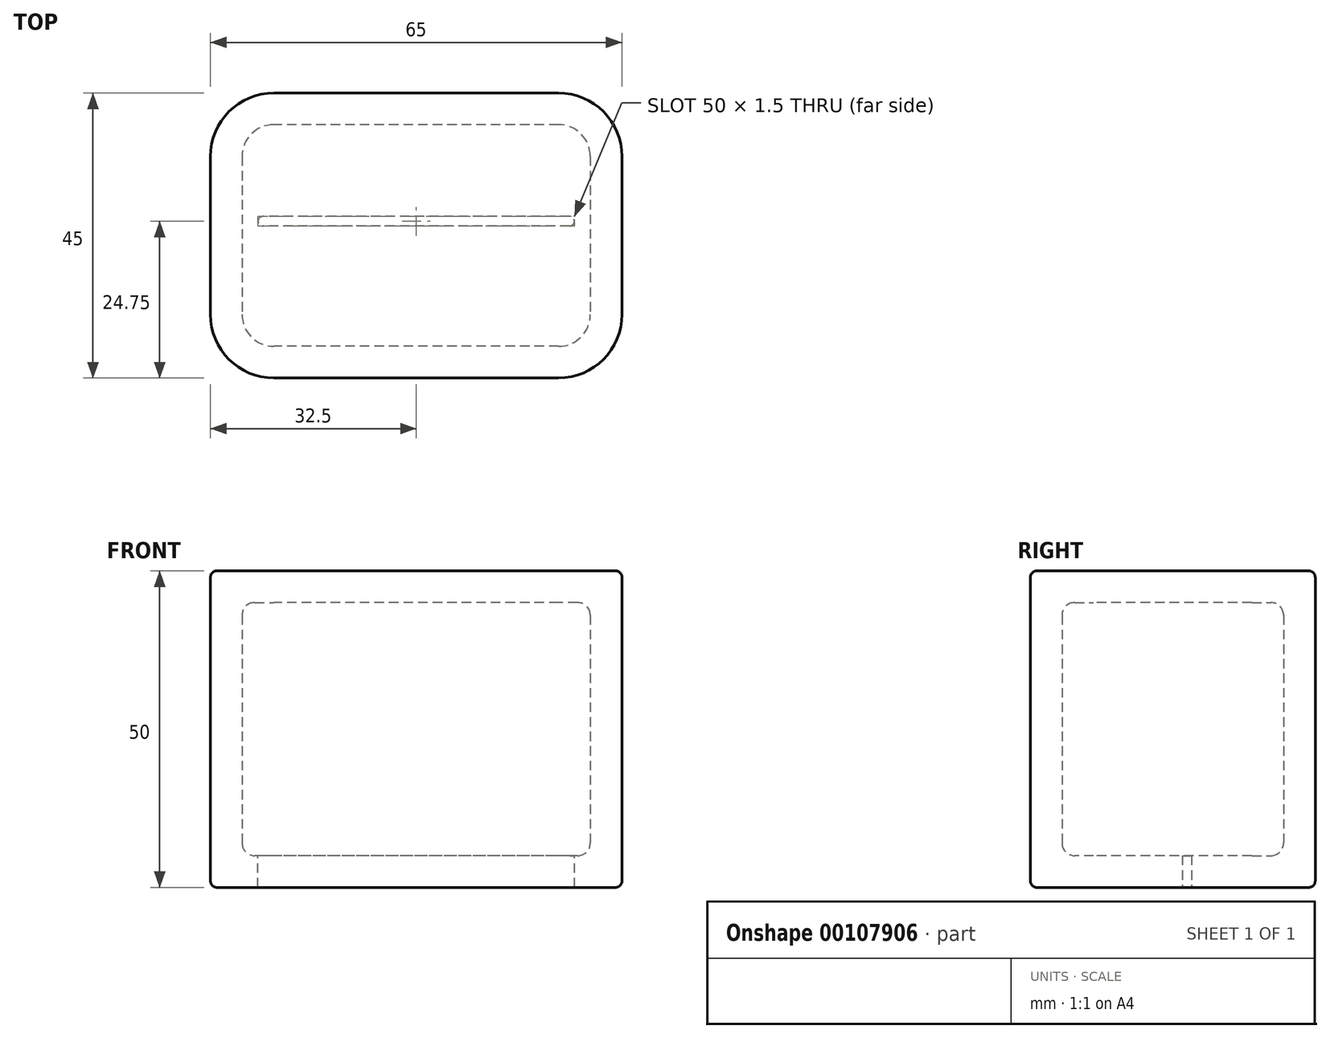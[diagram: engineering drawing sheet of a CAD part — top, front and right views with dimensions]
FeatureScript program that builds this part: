
annotation { "Feature Type Name" : "Feature", "Feature Type Description" : "" }
export const myFeature = defineFeature(function(context is Context, id is Id, definition is map)
    precondition{}
    {
        {
            var Q0;
            Q0=qCreatedBy(makeId("Top.planeOp"),FACE);
            var sketch = newSketch(context, id + "F0", { "sketchPlane" : qUnion([Q0])});
            skPoint(sketch, "E0.middle", {"position": v(0, 0) * mm});
            skLineSegment(sketch, "E1.bottom", {"start": v(32.5, 22.5) * mm, "end": v(-32.5, 22.5) * mm});
            skLineSegment(sketch, "E1.top", {"start": v(32.5, -22.5) * mm, "end": v(-32.5, -22.5) * mm});
            skLineSegment(sketch, "E1.left", {"start": v(32.5, 22.5) * mm, "end": v(32.5, -22.5) * mm});
            skLineSegment(sketch, "E1.right", {"start": v(-32.5, 22.5) * mm, "end": v(-32.5, -22.5) * mm});
            skLineSegment(sketch, "E2.bottom", {"start": v(-27.5, -17.5) * mm, "end": v(27.5, -17.5) * mm, "construction": true});
            skLineSegment(sketch, "E2.top", {"start": v(-27.5, 17.5) * mm, "end": v(27.5, 17.5) * mm, "construction": true});
            skLineSegment(sketch, "E2.left", {"start": v(-27.5, -17.5) * mm, "end": v(-27.5, 17.5) * mm, "construction": true});
            skLineSegment(sketch, "E2.right", {"start": v(27.5, -17.5) * mm, "end": v(27.5, 17.5) * mm, "construction": true});
            skLineSegment(sketch, "E3", {"start": v(-32.5, -17.5) * mm, "end": v(-27.5, -17.5) * mm, "construction": true});
            skLineSegment(sketch, "E4", {"start": v(-27.5, -17.5) * mm, "end": v(-27.5, -22.5) * mm, "construction": true});
            skSolve(sketch);
        }
        {
            var Q0;
            Q0=makeQuery(id+"F0.imprint","IMPRINT",FACE,{"disambiguationData":[TD([[makeQuery(id+"F0.imprint","IMPRINT",EDGE,{"derivedFrom":sQuery(id+"F0.wireOp",EDGE,"E1.bottom")}),1.0]])]});
            extrude(context, id + "F1", {"entities" : qUnion([Q0]), "depth" : 50 * mm});
        }
        {
            var Q0;
            Q0=makeQuery(id+"F1.opExtrude","SWEPT_EDGE",EDGE,{"disambiguationData":[OSD([sQuery(id+"F0.wireOp",EDGE,"E1.top"),sQuery(id+"F0.wireOp",EDGE,"E1.left")])]});
            var Q1;
            Q1=makeQuery(id+"F1.opExtrude","SWEPT_EDGE",EDGE,{"disambiguationData":[OSD([sQuery(id+"F0.wireOp",EDGE,"E1.top"),sQuery(id+"F0.wireOp",EDGE,"E1.right")])]});
            var Q2;
            Q2=makeQuery(id+"F1.opExtrude","SWEPT_EDGE",EDGE,{"disambiguationData":[OSD([sQuery(id+"F0.wireOp",EDGE,"E1.bottom"),sQuery(id+"F0.wireOp",EDGE,"E1.right")])]});
            var Q3;
            Q3=makeQuery(id+"F1.opExtrude","SWEPT_EDGE",EDGE,{"disambiguationData":[OSD([sQuery(id+"F0.wireOp",EDGE,"E1.bottom"),sQuery(id+"F0.wireOp",EDGE,"E1.left")])]});
            fillet(context, id + "F2", {"entities" : qUnion([Q0, Q1, Q2, Q3]), "radius" : 10 * mm, "tangentPropagation" : true, "allowEdgeOverflow" : false});
        }
        {
            var Q0;
            Q0=makeQuery(id+"F1.opExtrude","CAP_FACE",FACE,{"disambiguationData":[OSD([sQuery(id+"F0.wireOp",EDGE,"E1.bottom"),sQuery(id+"F0.wireOp",EDGE,"E1.top"),sQuery(id+"F0.wireOp",EDGE,"E1.left"),sQuery(id+"F0.wireOp",EDGE,"E1.right")])],"isStart":false});
            var Q1;
            Q1=makeQuery(id+"F1.opExtrude","SWEPT_BODY",BODY,{"disambiguationData":[OSD([sQuery(id+"F0.wireOp",EDGE,"E1.bottom"),sQuery(id+"F0.wireOp",EDGE,"E1.top"),sQuery(id+"F0.wireOp",EDGE,"E1.left"),sQuery(id+"F0.wireOp",EDGE,"E1.right")])]});
            shell(context, id + "F3", {"isHollow" : true, "entities" : qUnion([Q0]), "parts" : qUnion([Q1]), "thickness" : 5 * mm});
        }
        {
            var Q0;
            Q0=makeQuery(id+"F1.opExtrude","CAP_FACE",FACE,{"disambiguationData":[OSD([sQuery(id+"F0.wireOp",EDGE,"E1.bottom"),sQuery(id+"F0.wireOp",EDGE,"E1.top"),sQuery(id+"F0.wireOp",EDGE,"E1.left"),sQuery(id+"F0.wireOp",EDGE,"E1.right")])],"isStart":true});
            var sketch = newSketch(context, id + "F4", { "sketchPlane" : qUnion([Q0])});
            skLineSegment(sketch, "E5.bottom", {"start": v(25, -1.5) * mm, "end": v(-25, -1.5) * mm});
            skLineSegment(sketch, "E5.top", {"start": v(25, -3) * mm, "end": v(-25, -3) * mm});
            skLineSegment(sketch, "E5.left", {"start": v(25, -1.5) * mm, "end": v(25, -3) * mm});
            skLineSegment(sketch, "E5.right", {"start": v(-25, -1.5) * mm, "end": v(-25, -3) * mm});
            skSolve(sketch);
        }
        {
            var Q0;
            Q0=makeQuery(id+"F4.imprint","IMPRINT",FACE,{"disambiguationData":[TD([[makeQuery(id+"F4.imprint","IMPRINT",EDGE,{"derivedFrom":sQuery(id+"F4.wireOp",EDGE,"E5.bottom")}),1.0]])]});
            extrude(context, id + "F5", {"entities" : qUnion([Q0]), "operationType" : NewBodyOperationType.REMOVE, "endBound" : BoundingType.UP_TO_NEXT, "oppositeDirection" : true, "depth" : 11.66 * mm});
        }
        {
            var Q0;
            Q0=makeQuery(id+"F1.opExtrude","CAP_EDGE",EDGE,{"disambiguationData":[OSD([sQuery(id+"F0.wireOp",EDGE,"E1.top")])],"isStart":true});
            var Q1;
            Q1=makeQuery(id+"F1.opExtrude","CAP_FACE",FACE,{"disambiguationData":[OSD([sQuery(id+"F0.wireOp",EDGE,"E1.bottom"),sQuery(id+"F0.wireOp",EDGE,"E1.top"),sQuery(id+"F0.wireOp",EDGE,"E1.left"),sQuery(id+"F0.wireOp",EDGE,"E1.right")])],"isStart":false});
            fillet(context, id + "F6", {"entities" : qUnion([Q0, Q1]), "radius" : 1 * mm, "tangentPropagation" : true, "allowEdgeOverflow" : false});
        }
        {
            var Q0;
            Q0=makeQuery(id+"F5.boolean.opBoolean","COPY",EDGE,{"derivedFrom":makeQuery(id+"F5.opExtrude","SWEPT_EDGE",EDGE,{"disambiguationData":[OSD([sQuery(id+"F4.wireOp",EDGE,"E5.bottom"),sQuery(id+"F4.wireOp",EDGE,"E5.right")])]})});
            var Q1;
            Q1=makeQuery(id+"F5.boolean.opBoolean","COPY",EDGE,{"derivedFrom":makeQuery(id+"F5.opExtrude","SWEPT_EDGE",EDGE,{"disambiguationData":[OSD([sQuery(id+"F4.wireOp",EDGE,"E5.top"),sQuery(id+"F4.wireOp",EDGE,"E5.right")])]})});
            var Q2;
            Q2=makeQuery(id+"F5.boolean.opBoolean","COPY",EDGE,{"derivedFrom":makeQuery(id+"F5.opExtrude","SWEPT_EDGE",EDGE,{"disambiguationData":[OSD([sQuery(id+"F4.wireOp",EDGE,"E5.top"),sQuery(id+"F4.wireOp",EDGE,"E5.left")])]})});
            var Q3;
            Q3=makeQuery(id+"F5.boolean.opBoolean","COPY",EDGE,{"derivedFrom":makeQuery(id+"F5.opExtrude","SWEPT_EDGE",EDGE,{"disambiguationData":[OSD([sQuery(id+"F4.wireOp",EDGE,"E5.bottom"),sQuery(id+"F4.wireOp",EDGE,"E5.left")])]})});
            var Q4;
            Q4=makeQuery(id+"F5.boolean.opBoolean","COPY",EDGE,{"derivedFrom":makeQuery(id+"F5.opExtrude","CAP_EDGE",EDGE,{"disambiguationData":[OSD([sQuery(id+"F4.wireOp",EDGE,"E5.bottom")])],"isStart":true})});
            fillet(context, id + "F7", {"entities" : qUnion([Q0, Q1, Q2, Q3, Q4]), "radius" : .75 * mm, "tangentPropagation" : true, "allowEdgeOverflow" : false});
        }
        {
            var Q0;
            {var subQ0=sQuery(id+"F0.wireOp",EDGE,"E1.left");Q0=makeQuery(id+"F3.opShell","OFFSET_EDGE",EDGE,{"disambiguationData":[OSD([subQ0]),TDD([makeQuery(id+"F1.opExtrude","CAP_EDGE",EDGE,{"disambiguationData":[OSD([subQ0])],"isStart":true})])]});}
            var Q1;
            {var subQ0=sQuery(id+"F0.wireOp",EDGE,"E1.bottom");Q1=makeQuery(id+"F3.opShell","OFFSET_EDGE",EDGE,{"disambiguationData":[OSD([subQ0]),TDD([makeQuery(id+"F1.opExtrude","CAP_EDGE",EDGE,{"disambiguationData":[OSD([subQ0])],"isStart":false})])]});}
            fillet(context, id + "F8", {"entities" : qUnion([Q0, Q1]), "radius" : 2 * mm, "tangentPropagation" : true, "allowEdgeOverflow" : false});
        }
    });
